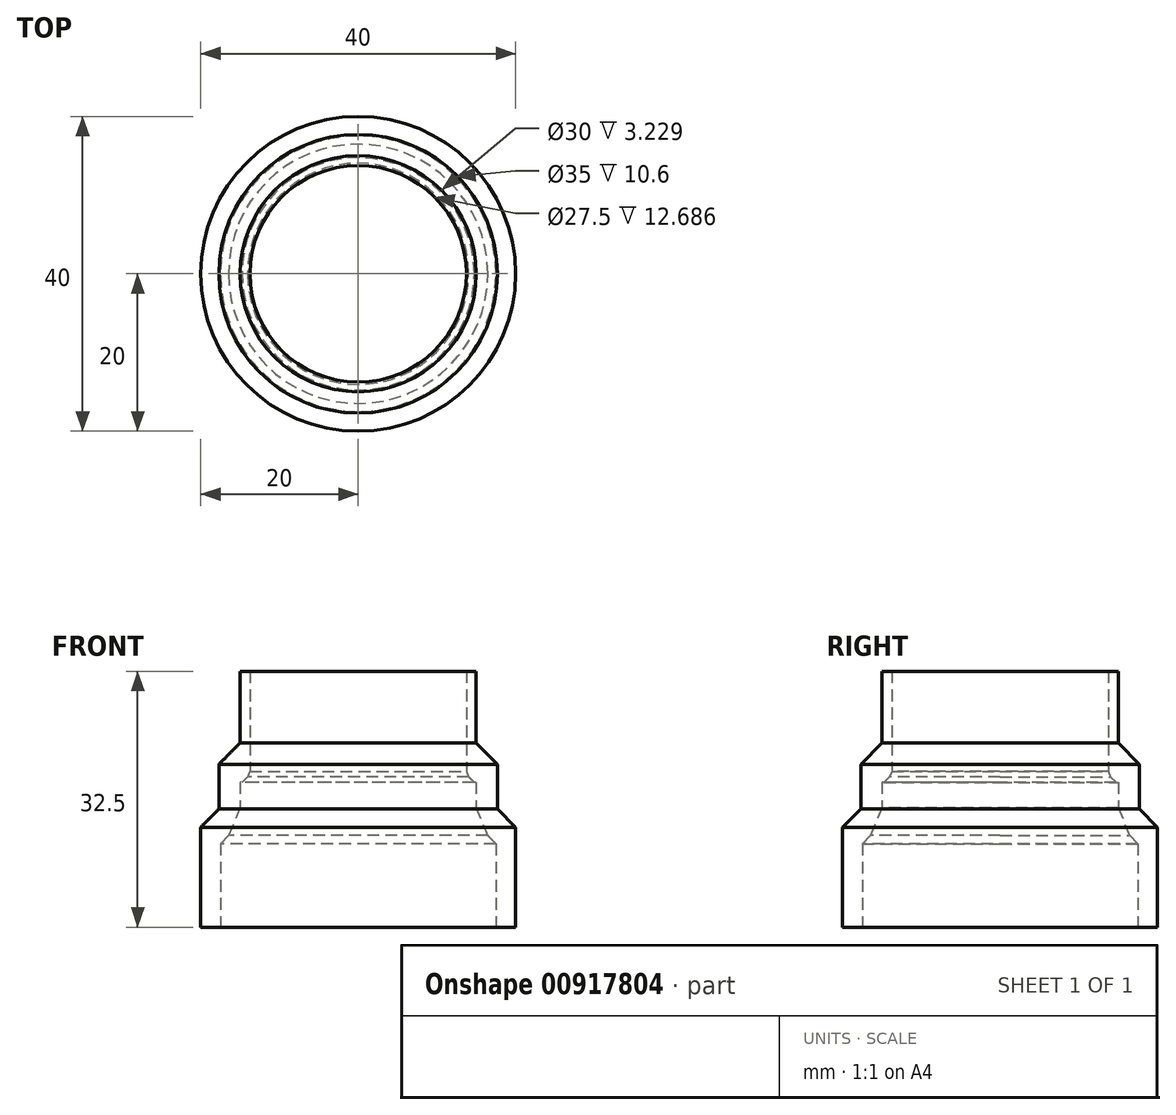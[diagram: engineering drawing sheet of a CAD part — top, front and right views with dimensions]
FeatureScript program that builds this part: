
annotation { "Feature Type Name" : "Feature", "Feature Type Description" : "" }
export const myFeature = defineFeature(function(context is Context, id is Id, definition is map)
    precondition{}
    {
        {
            var Q0;
            Q0=qCreatedBy(makeId("Top.planeOp"),FACE);
            var sketch = newSketch(context, id + "F0", { "sketchPlane" : qUnion([Q0])});
            skCircle(sketch, "E0", {"center": v(0, 0) * mm, "radius": 17.5 * mm});
            skCircle(sketch, "E1", {"center": v(0, 0) * mm, "radius": 20 * mm});
            skSolve(sketch);
        }
        {
            var Q0;
            Q0 = qSketchRegion(id + "F0", true);
            extrude(context, id + "F1", {"entities" : qUnion([Q0]), "depth" : 12 * mm, "offsetDistance" : 25 * mm});
        }
        {
            var Q0;
            Q0=qCreatedBy(makeId("Top.planeOp"),FACE);
            var Q1;
            Q1=makeQuery(id+"F1.opExtrude","CAP_FACE",FACE,{"disambiguationData":[OSD([sQuery(id+"F0.wireOp",EDGE,"E0"),sQuery(id+"F0.wireOp",EDGE,"E1")])],"isStart":false});
            var sketch = newSketch(context, id + "F2", { "sketchPlane" : qUnion([Q0, Q1])});
            skCircle(sketch, "E2", {"center": v(0, 0) * mm, "radius": 17.7 * mm});
            skCircle(sketch, "E3", {"center": v(0, 0) * mm, "radius": 13.75 * mm});
            skCircle(sketch, "E4", {"center": v(0, 0) * mm, "radius": 15 * mm});
            skSolve(sketch);
        }
        {
            var Q0;
            Q0 = qSketchRegion(id + "F2", true);
            extrude(context, id + "F3", {"entities" : qUnion([Q0]), "operationType" : NewBodyOperationType.ADD, "depth" : 23.7 * mm, "offsetDistance" : 25 * mm, "hasSecondDirection" : true, "secondDirectionOppositeDirection" : false, "secondDirectionDepth" : 10.6 * mm});
        }
        {
            var Q0;
            Q0=qCreatedBy(makeId("Top.planeOp"),FACE);
            var sketch = newSketch(context, id + "F4", { "sketchPlane" : qUnion([Q0])});
            skCircle(sketch, "E5", {"center": v(0, 0) * mm, "radius": 15 * mm});
            skCircle(sketch, "E6", {"center": v(0, 0) * mm, "radius": 13.75 * mm});
            skSolve(sketch);
        }
        {
            var Q0;
            Q0 = qSketchRegion(id + "F4", true);
            extrude(context, id + "F5", {"entities" : qUnion([Q0]), "operationType" : NewBodyOperationType.ADD, "depth" : 32.5 * mm, "offsetDistance" : 25 * mm, "hasSecondDirection" : true, "secondDirectionOppositeDirection" : false, "secondDirectionDepth" : 18.4 * mm});
        }
        {
            var Q0;
            Q0=makeQuery(id+"F3.opExtrude","CAP_EDGE",EDGE,{"disambiguationData":[OSD([sQuery(id+"F2.wireOp",EDGE,"E4")])],"isStart":true});
            chamfer(context, id + "F6", {"entities" : qUnion([Q0]), "width" : 2.5 * mm, "tangentPropagation" : true});
        }
        {
            var Q0;
            Q0=makeQuery(id+"F5.opExtrude","CAP_EDGE",EDGE,{"disambiguationData":[OSD([sQuery(id+"F4.wireOp",EDGE,"E6")])],"isStart":true});
            chamfer(context, id + "F7", {"entities" : qUnion([Q0]), "width" : 1 * mm, "tangentPropagation" : true});
        }
        {
            var Q0;
            {var subQ0=sQuery(id+"F2.wireOp",EDGE,"E4");Q0=makeQuery(id+"F6.opChamfer","BLEND_EDGE",EDGE,{"blendedFrom":[makeQuery(id+"F3.opExtrude","CAP_EDGE",EDGE,{"disambiguationData":[OSD([subQ0])],"isStart":true}),makeQuery(id+"F3.opExtrude","SWEPT_FACE",FACE,{"disambiguationData":[OSD([subQ0])]})],"blendedInto":[makeQuery(id+"F3.opExtrude","SWEPT_FACE",FACE,{"disambiguationData":[OSD([subQ0])]})]});}
            chamfer(context, id + "F8", {"entities" : qUnion([Q0]), "width" : 5 * mm, "tangentPropagation" : true});
        }
        {
            var Q0;
            {var subQ0=sQuery(id+"F4.wireOp",EDGE,"E6");Q0=makeQuery(id+"F7.opChamfer","BLEND_EDGE",EDGE,{"blendedFrom":[makeQuery(id+"F5.opExtrude","CAP_EDGE",EDGE,{"disambiguationData":[OSD([subQ0])],"isStart":true}),makeQuery(id+"F5.opExtrude","SWEPT_FACE",FACE,{"disambiguationData":[OSD([subQ0])]})],"blendedInto":[makeQuery(id+"F5.opExtrude","SWEPT_FACE",FACE,{"disambiguationData":[OSD([subQ0])]})]});}
            chamfer(context, id + "F9", {"entities" : qUnion([Q0]), "width" : 1 * mm, "tangentPropagation" : true});
        }
        {
            var Q0;
            Q0=makeQuery(id+"F3.boolean.opBoolean","INTERSECT",EDGE,{"derivedFrom":[makeQuery(id+"F1.opExtrude","CAP_FACE",FACE,{"disambiguationData":[OSD([sQuery(id+"F0.wireOp",EDGE,"E0"),sQuery(id+"F0.wireOp",EDGE,"E1")])],"isStart":false}),makeQuery(id+"F3.opExtrude","SWEPT_FACE",FACE,{"disambiguationData":[OSD([sQuery(id+"F2.wireOp",EDGE,"E2")])]})]});
            var Q1;
            Q1=makeQuery(id+"F3.opExtrude","CAP_EDGE",EDGE,{"disambiguationData":[OSD([sQuery(id+"F2.wireOp",EDGE,"E2")])],"isStart":false});
            chamfer(context, id + "F10", {"entities" : qUnion([Q0, Q1]), "width" : 3 * mm, "tangentPropagation" : true});
        }
    });
